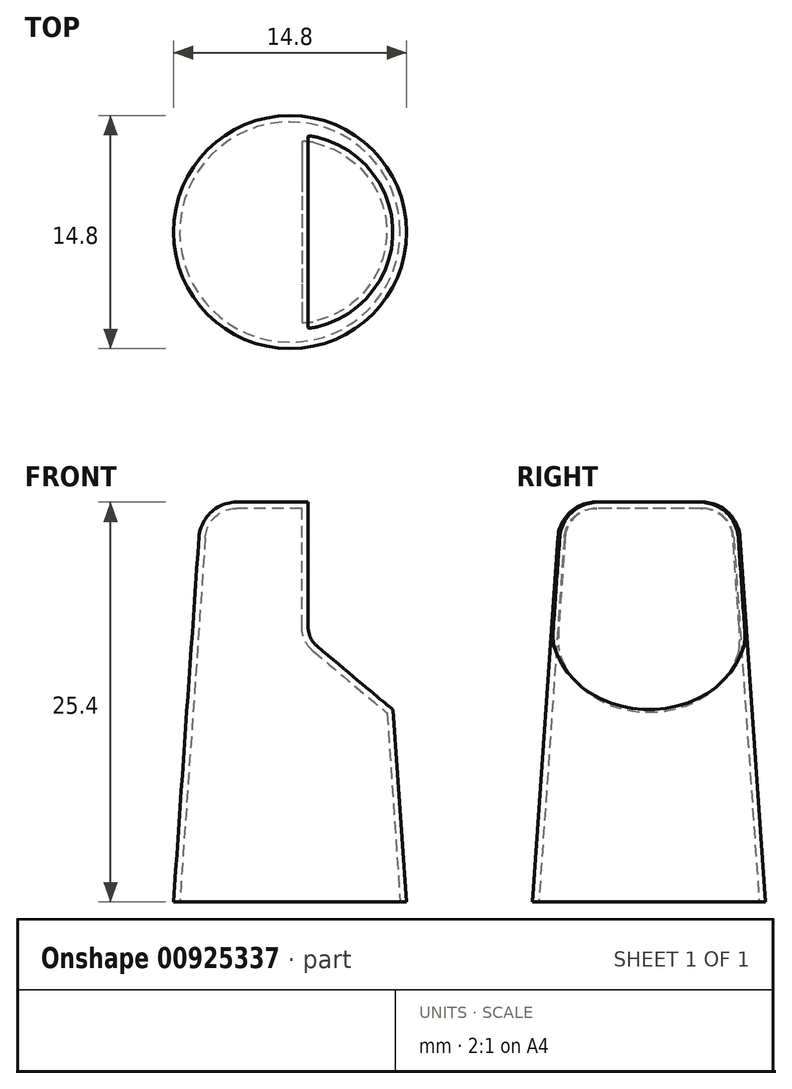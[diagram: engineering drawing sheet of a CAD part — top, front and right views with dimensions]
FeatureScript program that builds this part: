
annotation { "Feature Type Name" : "Feature", "Feature Type Description" : "" }
export const myFeature = defineFeature(function(context is Context, id is Id, definition is map)
    precondition{}
    {
        {
            var Q0;
            Q0=qCreatedBy(makeId("Front.planeOp"),FACE);
            var sketch = newSketch(context, id + "F0", { "sketchPlane" : qUnion([Q0])});
            skLineSegment(sketch, "E0", {"start": v(0, 0) * mm, "end": v(0, 25) * mm});
            skLineSegment(sketch, "E1", {"start": v(0, 0) * mm, "end": v(7, 0) * mm});
            skLineSegment(sketch, "E2", {"start": v(7, 0) * mm, "end": v(5.25, 25) * mm});
            skLineSegment(sketch, "E3", {"start": v(5.25, 25) * mm, "end": v(0, 25) * mm});
            skSolve(sketch);
        }
        {
            var Q0;
            Q0 = qSketchRegion(id + "F0", true);
            var Q1;
            Q1=sQuery(id+"F0.wireOp",EDGE,"E0");
            revolve(context, id + "F1", {"surfaceOperationType" : NewSurfaceOperationType.NEW, "entities" : qUnion([Q0]), "axis" : qUnion([Q1]), "revolveType" : RevolveType.FULL});
        }
        {
            var Q0;
            Q0=makeQuery(id+"F1.opRevolve","SWEPT_EDGE",EDGE,{"disambiguationData":[OSD([sQuery(id+"F0.wireOp",EDGE,"E2"),sQuery(id+"F0.wireOp",EDGE,"E3")])]});
            fillet(context, id + "F2", {"entities" : qUnion([Q0]), "radius" : 2 * mm, "tangentPropagation" : true, "allowEdgeOverflow" : false});
        }
        {
            var Q0;
            Q0=qCreatedBy(makeId("Front.planeOp"),FACE);
            var sketch = newSketch(context, id + "F3", { "sketchPlane" : qUnion([Q0])});
            skLineSegment(sketch, "E4.0", {"start": v(5.25, 25) * mm, "end": v(0.75, 25) * mm});
            skLineSegment(sketch, "E5", {"start": v(5.25, 25) * mm, "end": v(6.16, 12) * mm});
            skLineSegment(sketch, "E6", {"start": v(0.75, 25) * mm, "end": v(0.75, 17.47) * mm});
            skArc(sketch, "E7", {"start": v(0.75, 17.47) * mm, "mid": v(0.94, 16.63) * mm, "end": v(1.46, 15.94) * mm});
            skLineSegment(sketch, "E8", {"start": v(1.46, 15.94) * mm, "end": v(6.16, 12) * mm});
            skLineSegment(sketch, "E9", {"start": v(0, 0) * mm, "end": v(0, 19.97) * mm, "construction": true});
            skSolve(sketch);
        }
        {
            var Q0;
            Q0 = qSketchRegion(id + "F3", true);
            extrude(context, id + "F4", {"entities" : qUnion([Q0]), "operationType" : NewBodyOperationType.REMOVE, "endBound" : BoundingType.THROUGH_ALL, "oppositeDirection" : true, "depth" : 25 * mm, "offsetDistance" : 25 * mm, "hasSecondDirection" : true, "secondDirectionBound" : SecondDirectionBoundingType.THROUGH_ALL, "secondDirectionOppositeDirection" : false, "secondDirectionDepth" : 25 * mm});
        }
        {
            var Q0;
            Q0=makeQuery(id+"F1.opRevolve","SWEPT_FACE",FACE,{"disambiguationData":[OSD([sQuery(id+"F0.wireOp",EDGE,"E1")])]});
            shell(context, id + "F5", {"entities" : qUnion([Q0]), "thickness" : 0.4 * mm, "oppositeDirection" : true});
        }
    });
